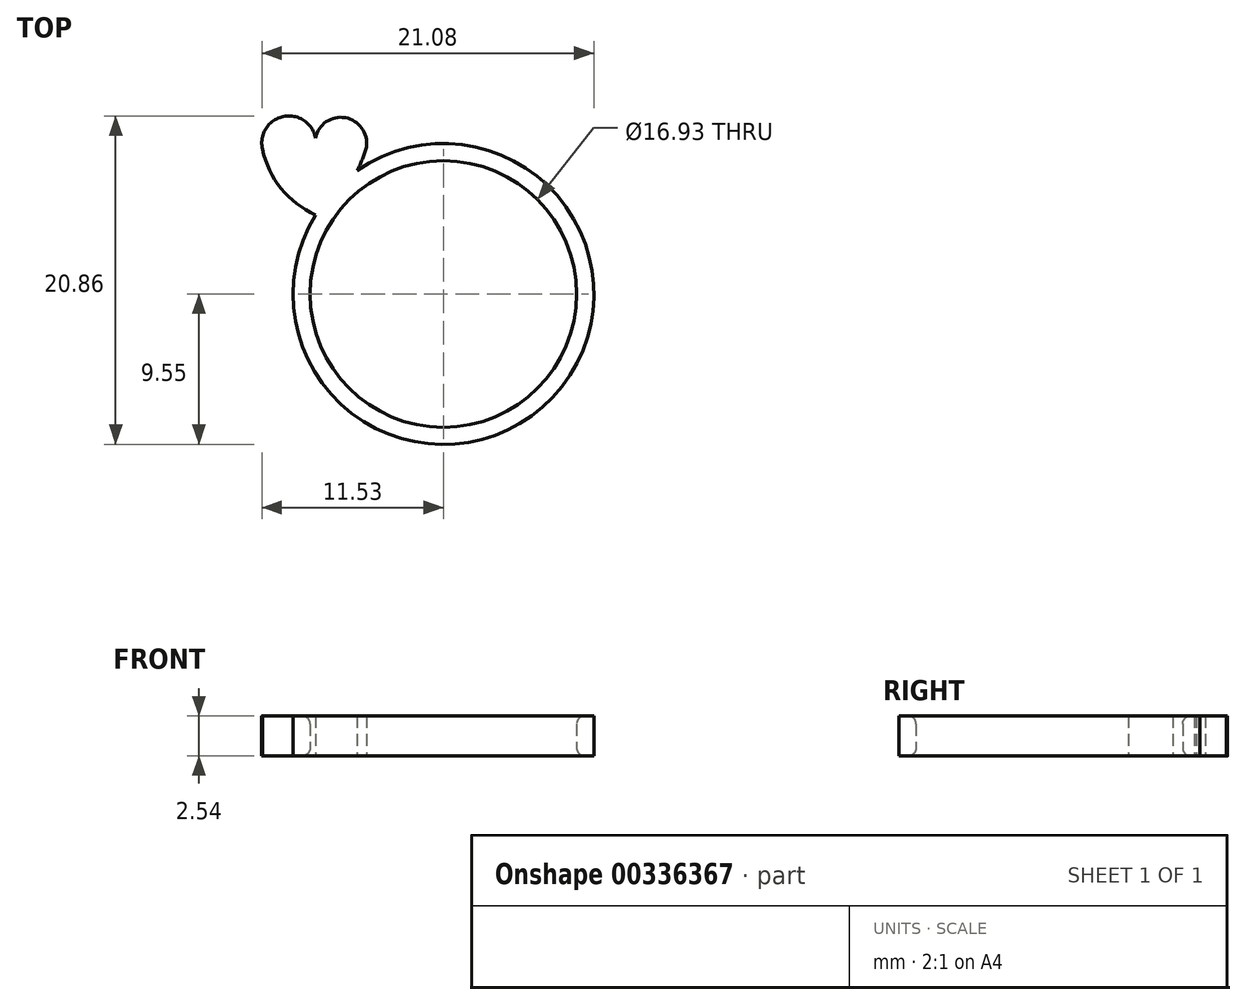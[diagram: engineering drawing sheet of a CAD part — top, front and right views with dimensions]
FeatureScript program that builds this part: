
annotation { "Feature Type Name" : "Feature", "Feature Type Description" : "" }
export const myFeature = defineFeature(function(context is Context, id is Id, definition is map)
    precondition{}
    {
        {
            var Q0;
            Q0=qCreatedBy(makeId("Top.planeOp"),FACE);
            var sketch = newSketch(context, id + "F0", { "sketchPlane" : qUnion([Q0])});
            skCircle(sketch, "E0", {"center": v(0, 0) * mm, "radius": 8.46 * mm});
            skArc(sketch, "E1", {"start": v(-8.13, 5.03) * mm, "mid": v(6.95, -6.56) * mm, "end": v(-5.48, 7.83) * mm});
            skArc(sketch, "E2", {"start": v(-5.48, 7.83) * mm, "mid": v(-5.14, 8.57) * mm, "end": v(-4.9, 9.34) * mm});
            skArc(sketch, "E3", {"start": v(-11.49, 9.2) * mm, "mid": v(-10.3, 6.7) * mm, "end": v(-8.13, 5.03) * mm});
            skArc(sketch, "E4", {"start": v(-8.12, 9.9) * mm, "mid": v(-10.17, 11.28) * mm, "end": v(-11.49, 9.2) * mm});
            skArc(sketch, "E5", {"start": v(-4.9, 9.34) * mm, "mid": v(-6.23, 11.2) * mm, "end": v(-8.12, 9.9) * mm});
            skSolve(sketch);
        }
        {
            var Q0;
            Q0=makeQuery(id+"F0.imprint","IMPRINT",FACE,{"disambiguationData":[TD([[makeQuery(id+"F0.imprint","IMPRINT",EDGE,{"derivedFrom":sQuery(id+"F0.wireOp",EDGE,"E0")}),-1.0]])]});
            extrude(context, id + "F1", {"entities" : qUnion([Q0]), "depth" : 2.54 * mm});
        }
        {
            var Q0;
            Q0=makeQuery(id+"F1.opExtrude","CAP_EDGE",EDGE,{"disambiguationData":[OSD([sQuery(id+"F0.wireOp",EDGE,"E0")])],"isStart":true});
            var Q1;
            Q1=makeQuery(id+"F1.opExtrude","CAP_EDGE",EDGE,{"disambiguationData":[OSD([sQuery(id+"F0.wireOp",EDGE,"E0")])],"isStart":false});
            fillet(context, id + "F2", {"entities" : qUnion([Q0, Q1]), "radius" : 0.5 * mm, "tangentPropagation" : true, "allowEdgeOverflow" : false});
        }
    });
